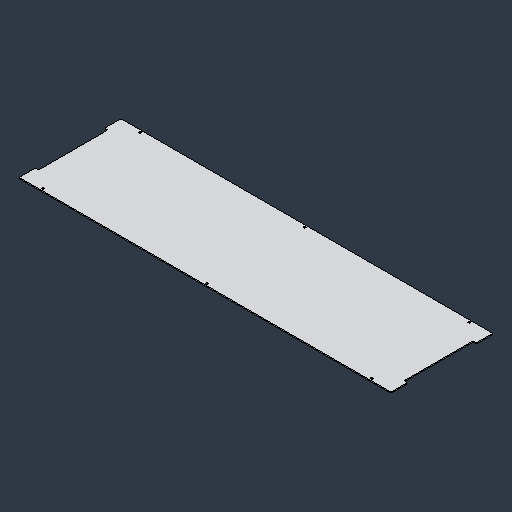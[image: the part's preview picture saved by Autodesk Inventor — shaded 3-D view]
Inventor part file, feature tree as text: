
AUTODESK INVENTOR PART (.ipt)
format: ipt  version: 2024.3 (Build 283343000, 343)  size: 96,768 bytes
history: native  units: mm (DEFAULTED — no unit token found)
features: fillet x1
ambient origin geometry x8: Origin, YZ Plane, XZ Plane, XY Plane, X Axis, Y Axis, Z Axis, Center Point
bodies: Solid1 (feature_tree)
feature tree (1):
  fillet  "Fillet2"  [1 undecoded]
note: 1 required parameter value undecoded (feature->parameter linkage not recoverable at this tier; creation-order binding heuristic only, values carry confidence <= 0.55)
